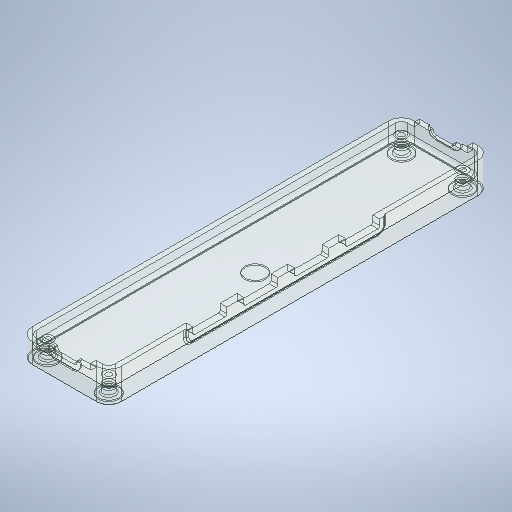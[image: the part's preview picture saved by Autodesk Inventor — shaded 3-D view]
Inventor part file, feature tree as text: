
AUTODESK INVENTOR PART (.ipt)
format: ipt  version: 2025.1 (Build 291241020, 241B)  size: 686,080 bytes
history: native  units: mm
features: extrude x16, sketch x10, other x6, fillet x4, chamfer x1
ambient origin geometry x8: Origin, YZ Plane, XZ Plane, XY Plane, X Axis, Y Axis, Z Axis, Center Point
bodies: Body1 (feature_tree)
feature tree (37):
  other  "Sólido1"
  sketch  "Esboço1"  dims[d0=145.0mm d1=30.0mm]
  extrude  "Extrusão1"  Depth=30.0mm
  extrude  "Extrusão3"  Depth=3.0mm
  extrude  "Extrusão4"  Depth=3.0mm
  extrude  "Extrusão5"  Depth=4.3mm
  sketch  "Esboço3"  dims[d2=3.0mm d3=3.0mm]
  extrude  "Extrusão6"  Depth=2.0mm TaperAngle=0.0deg
  extrude  "Extrusão7"  Depth=2.0mm TaperAngle=0.0deg
  sketch  "Esboço4"  dims[d4=2.2mm d6=3.0mm]
  extrude  "Extrusão8"  Depth=145.0mm
  extrude  "Extrusão9"  Depth=2.0mm
  extrude  "Extrusão10"  Depth=2.5mm
  extrude  "Extrusão11"  Depth=146.0mm
  extrude  "Extrusão12"  Depth=2.5mm
  extrude  "Extrusão13"  Depth=0.52mm TaperAngle=0.0deg
  fillet  "Arredondamento1"  Radius=5.0mm
  fillet  "Arredondamento3"  Radius=7.682mm
  extrude  "Extrusão15"  Depth=4.103mm TaperAngle=0.0deg
  fillet  "Arredondamento5"  Radius=7.0mm
  extrude  "Extrusão16"  Depth=7.0mm
  chamfer  "Chanfro1"  Distance=7.0mm
  fillet  "Arredondamento6"  Radius=1.613mm
  extrude  "Extrusão17"  Depth=9.24mm
  extrude  "Extrusão18"  Depth=5.868mm
  other  "Contorno projetado1"
  sketch  "Esboço5"  dims[d7=3.0mm d8=4.3mm]
  sketch  "Esboço6"  dims[d9=2.0mm d10=3.0mm d11=0.0mm]
  sketch  "Esboço7"  dims[d14=6.0mm d15=0.0mm d16=2.0mm d17=0.0mm]
  sketch  "Esboço8"  dims[d18=6.0mm d19=0.0mm d20=145.0mm]
  other  "Contorno projetado2"
  sketch  "Esboço9"  dims[d21=30.0mm d22=2.0mm]
  other  "Contorno projetado3"
  sketch  "Esboço10"  dims[d23=2.5mm d24=2.5mm]
  other  "Contorno projetado4"
  sketch  "Esboço11"  dims[d25=31.0mm d26=146.0mm d27=2.5mm d28=3.0mm d29=0.0mm d30=5.0mm d31=7.682mm d32=0.0mm d35=4.103mm d36=0.0mm d37=7.0mm d38=7.0mm d39=7.0mm d40=1.613mm d41=0.0mm d42=9.24mm d44=5.868mm d45=7.66mm d46=1.45mm d47=1.613mm d48=0.0mm d49=1.688mm d50=0.0mm d51=9.24mm d52=5.88mm d53=1.82mm d54=1.45mm d55=1.688mm d56=0.0mm d57=5.892mm d58=13.4mm d59=2.995mm d60=6.6mm d61=6.6mm d62=6.6mm d63=32.37mm d64=44.23mm d65=0.75mm d66=10.0mm d67=0.0mm d68=0.5mm d70=7.8mm d73=1.5mm d75=8.0mm d76=0.5mm d77=0.0mm d78=0.3mm d79=8.0mm d84=0.65mm d85=0.0mm d86=0.65mm d87=2.0mm d88=45.0deg d89=1.0mm d97=2.0mm d98=2.0mm d99=2.0mm d100=2.375mm d101=1.75mm d102=1.75mm d103=1.75mm d104=3.2mm d105=0.52mm d106=0.0mm d107=1.75mm d108=1.75mm d109=1.75mm d110=3.2mm d111=0.52mm d112=0.0mm d43=0.872665mm]
  other  "Contorno projetado5"
